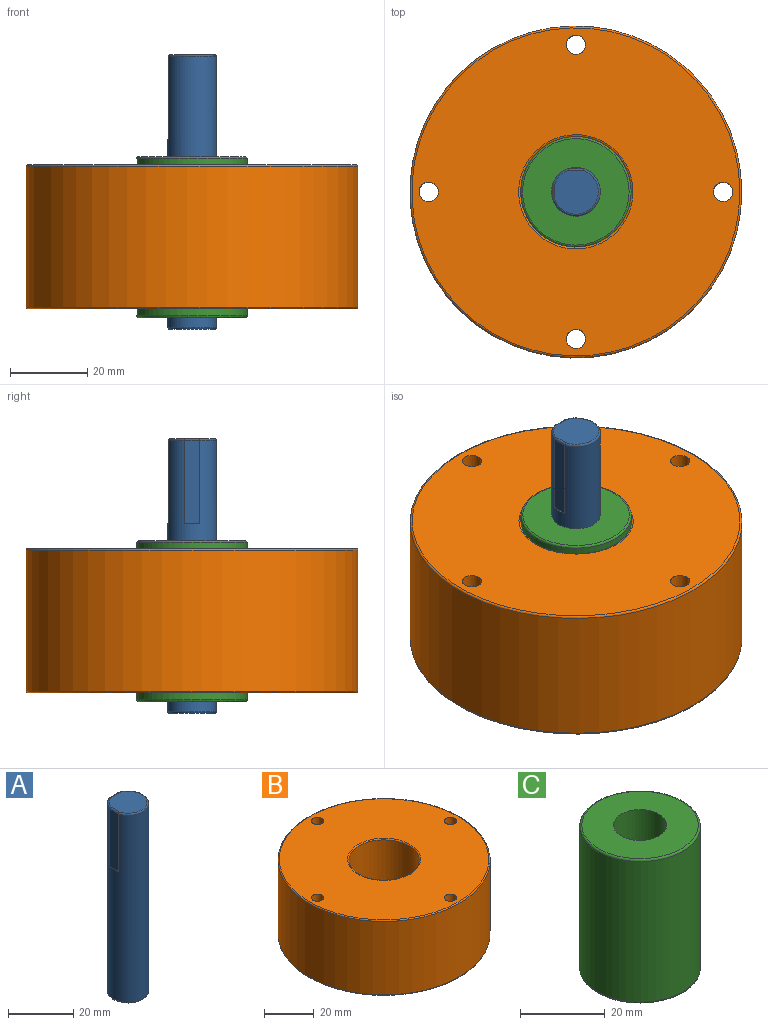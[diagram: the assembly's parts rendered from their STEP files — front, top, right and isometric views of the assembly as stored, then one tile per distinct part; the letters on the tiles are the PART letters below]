
ASSEMBLY  parts=3 mates=2
PART A: 12 faces, bbox 13.6x13.6x71 mm
  f0: cylinder r=6.3mm len=70mm, axis (0,0,-1), area 2603mm2, adj f3,f4,f5,f6,f7,f10,f11
  f1: plane 11.3x11.3mm, normal (0,0,1), area 104.2mm2, adj f7,f8,f9,f10
  f2: plane 11.6x11.6mm, normal (0,0,-1), area 105.7mm2, adj f11
  f3: plane 3.84x0.3mm, normal (0,0,1), area 0.8mm2, adj f0,f4
  f4: plane 21.5x3.84mm, normal (0,1,0), area 82.6mm2, adj f0,f3,f9
  f5: plane 3.84x0.3mm, normal (0,0,1), area 0.8mm2, adj f0,f6
  f6: plane 21.5x3.84mm, normal (-1,0,0), area 82.6mm2, adj f0,f5,f8
  f7: torus R=5.8mm, axis (0,0,1), area 4.5mm2, adj f0,f1,f8,f9
  f8: cylinder r=0.5mm len=3.84mm, axis (0,-1,0), area 3mm2, adj f1,f6,f7,f10
  f9: cylinder r=0.5mm len=3.84mm, axis (-1,0,0), area 3mm2, adj f1,f4,f7,f10
  f10: torus R=5.8mm, axis (0,0,1), area 19.6mm2, adj f0,f1,f8,f9
  f11: torus R=5.8mm, axis (0,0,1), area 30.2mm2, adj f0,f2
PART B: 12 faces, bbox 92.8x92.8x37.3 mm
  f0: cylinder r=14.25mm len=36.3mm, axis (0,0,-1), area 3250.1mm2, adj f4,f6
  f1: cylinder r=42.85mm len=85.7mm, axis (0,0,-1), area 9773.2mm2, adj f5,f7
  f2: plane 84.7x84.7mm, normal (0,0,1), area 4872.5mm2, adj f6,f7,f8,f9,f10,f11
  f3: plane 84.7x84.7mm, normal (0,0,-1), area 4872.5mm2, adj f4,f5,f8,f9,f10,f11
  f4: torus R=14.75mm, axis (0,0,1), area 71.2mm2, adj f0,f3
  f5: torus R=42.35mm, axis (0,0,1), area 210.6mm2, adj f1,f3
  f6: torus R=14.75mm, axis (0,0,1), area 71.2mm2, adj f0,f2
  f7: torus R=42.35mm, axis (0,0,1), area 210.6mm2, adj f1,f2
  f8: cylinder r=2.5mm len=37.3mm, axis (0,0,1), area 585.9mm2, adj f2,f3
  f9: cylinder r=2.5mm len=37.3mm, axis (0,0,1), area 585.9mm2, adj f2,f3
  f10: cylinder r=2.5mm len=37.3mm, axis (0,0,1), area 585.9mm2, adj f2,f3
  f11: cylinder r=2.5mm len=37.3mm, axis (0,0,1), area 585.9mm2, adj f2,f3
PART C: 6 faces, bbox 30.8x30.8x41.6 mm
  f0: cylinder r=14.25mm len=40.6mm, axis (0,0,-1), area 3635.1mm2, adj f3,f4
  f1: plane 27.5x27.5mm, normal (0,0,1), area 469.3mm2, adj f4,f5
  f2: plane 27.5x27.5mm, normal (0,0,-1), area 469.3mm2, adj f3,f5
  f3: torus R=13.75mm, axis (0,0,1), area 69.4mm2, adj f0,f2
  f4: torus R=13.75mm, axis (0,0,1), area 69.4mm2, adj f0,f1
  f5: cylinder r=6.3mm len=41.6mm, axis (0,0,1), area 1646.7mm2, adj f1,f2
PLACE A t=(-37.45,-12.55,-10.34)mm
PLACE B t=(-37.45,-12.55,-5.04)mm
PLACE C t=(-37.45,-12.55,-7.34)mm
MATE revolute A.f0 <-> C.f5  axis (0,0,-1) through (-37.45,-12.55,-10.34)mm
MATE fastened C.f0 <-> B.f1  axis (0,0,-1) through (-37.45,-12.55,-7.34)mm
